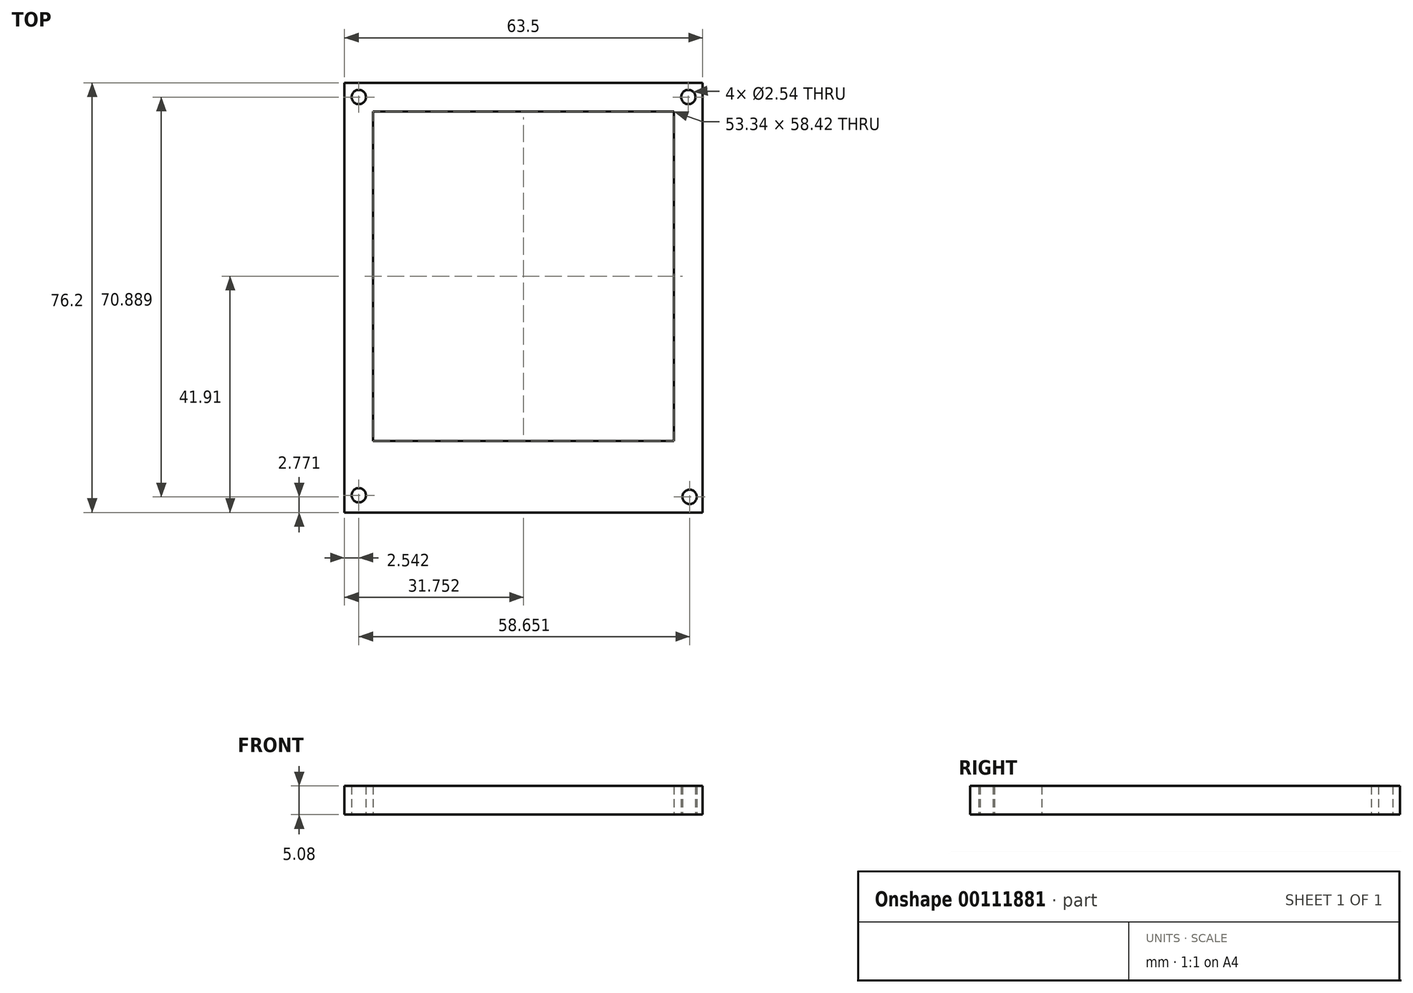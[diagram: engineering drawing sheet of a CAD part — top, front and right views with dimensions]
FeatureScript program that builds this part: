
annotation { "Feature Type Name" : "Feature", "Feature Type Description" : "" }
export const myFeature = defineFeature(function(context is Context, id is Id, definition is map)
    precondition{}
    {
        {
            var Q0;
            Q0=qCreatedBy(makeId("Top.planeOp"),FACE);
            var sketch = newSketch(context, id + "F0", { "sketchPlane" : qUnion([Q0])});
            skLineSegment(sketch, "E0.bottom", {"start": v(-40.88, 34.12) * mm, "end": v(22.62, 34.12) * mm});
            skLineSegment(sketch, "E0.top", {"start": v(-40.88, -42.08) * mm, "end": v(22.62, -42.08) * mm});
            skLineSegment(sketch, "E0.left", {"start": v(-40.88, 34.12) * mm, "end": v(-40.88, -42.08) * mm});
            skLineSegment(sketch, "E0.right", {"start": v(22.62, 34.12) * mm, "end": v(22.62, -42.08) * mm});
            skLineSegment(sketch, "E1", {"start": v(-40.88, 34.12) * mm, "end": v(22.62, -42.08) * mm, "construction": true});
            skLineSegment(sketch, "E2", {"start": v(22.62, 34.12) * mm, "end": v(-40.88, -42.08) * mm, "construction": true});
            skLineSegment(sketch, "E3.top", {"start": v(-40.88, 29.04) * mm, "end": v(22.62, 29.04) * mm});
            skLineSegment(sketch, "E3.left", {"start": v(-40.88, 34.12) * mm, "end": v(-40.88, 29.04) * mm});
            skLineSegment(sketch, "E3.right", {"start": v(22.62, 34.12) * mm, "end": v(22.62, 29.04) * mm});
            skLineSegment(sketch, "E4.bottom", {"start": v(-40.88, 34.12) * mm, "end": v(-35.8, 34.12) * mm});
            skLineSegment(sketch, "E4.top", {"start": v(-40.88, -42.08) * mm, "end": v(-35.8, -42.08) * mm});
            skLineSegment(sketch, "E4.right", {"start": v(-35.8, 34.12) * mm, "end": v(-35.8, -42.08) * mm});
            skLineSegment(sketch, "E5.bottom", {"start": v(22.62, 34.12) * mm, "end": v(17.54, 34.12) * mm});
            skLineSegment(sketch, "E5.top", {"start": v(22.62, -42.08) * mm, "end": v(17.54, -42.08) * mm});
            skLineSegment(sketch, "E5.right", {"start": v(17.54, 34.12) * mm, "end": v(17.54, -42.08) * mm});
            skLineSegment(sketch, "E6.top", {"start": v(-40.88, -29.38) * mm, "end": v(22.62, -29.38) * mm});
            skLineSegment(sketch, "E6.left", {"start": v(-40.88, -42.08) * mm, "end": v(-40.88, -29.38) * mm});
            skLineSegment(sketch, "E6.right", {"start": v(22.62, -42.08) * mm, "end": v(22.62, -29.38) * mm});
            skLineSegment(sketch, "E7", {"start": v(-40.88, -37) * mm, "end": v(22.62, -37) * mm, "construction": true});
            skLineSegment(sketch, "E8", {"start": v(-40.88, -37) * mm, "end": v(-35.8, -42.08) * mm, "construction": true});
            skLineSegment(sketch, "E9", {"start": v(22.62, -37) * mm, "end": v(17.54, -42.08) * mm, "construction": true});
            skLineSegment(sketch, "E10", {"start": v(17.54, 34.12) * mm, "end": v(22.62, 29.04) * mm, "construction": true});
            skLineSegment(sketch, "E11", {"start": v(-35.8, 34.12) * mm, "end": v(-40.88, 29.04) * mm, "construction": true});
            skCircle(sketch, "E12", {"center": v(-38.34, -39.03) * mm, "radius": 1.27 * mm});
            skPoint(sketch, "E12.centerSnap0", {"position": v(-38.34, -39.54) * mm});
            skCircle(sketch, "E13", {"center": v(20.31, -39.3) * mm, "radius": 1.27 * mm});
            skCircle(sketch, "E14", {"center": v(20.08, 31.58) * mm, "radius": 1.27 * mm});
            skCircle(sketch, "E15", {"center": v(-38.34, 31.58) * mm, "radius": 1.27 * mm});
            skSolve(sketch);
        }
        {
            var Q0;
            Q0 = qSketchRegion(id + "F0", true);
            extrude(context, id + "F1", {"entities" : qUnion([Q0]), "depth" : 5.08 * mm});
        }
    });
